# Revit family: Weitspannkabelleiter - WKLG 1160 FT,FS,FSK,FTSO,A2,A4
name_source: partatom
category: Generic Models
revit_build: Autodesk Revit 2017 (Build: 20190508_0315(x64)
units: mm (PartAtom-declared; Revit-internal decimal feet)

## family parameters
Always vertical = Yes
Can host rebar = No
Cut with Voids When Loaded = No
Part Type = Normal
Room Calculation Point = No
Round Connector Dimension = Use Diameter
Shared = No
Work Plane-Based = No

## types (6) — shared parameters
Cut's space = 75 mm
Cut's space 2 = 300 mm  [stored 0.984252 ft]
Cut's space 3 = 3000 mm  [stored 9.84252 ft]
Height = 110 mm  [stored 0.360892 ft]
Height 1 = 168 mm  [stored 0.551181 ft]
Length 1 = 773 mm  [stored 2.53609 ft]
Manufacturer = OBO Bettermann
URL = http://www.obo-bettermann.com
Width = 35 mm  [stored 0.114829 ft]
Width 1 = 600 mm
Width 2 = 300 mm  [stored 0.984252 ft]

## per-type parameters (varying)
| type | Cut's number | Cut's number 2 | Cut's number 3 | GTIN | Length | Manufacturer Art.No. | Material |
| WKLG 1160 FT | 120 | 30 | 3 | 4012196883578 | 9000 mm | 6311075 | Hot-dip galvanised |
| WKLG 1160 FS | 80 | 20 | 2 | 4012196883271 | 6000 mm  [stored 19.685 ft] | 6311024 | Strip-galvanised |
| WKLG 1160 FT SO | 80 | 20 | 2 | 4012195753056 | 6000 mm  [stored 19.685 ft] | 7189022 | Hot-dip galvanised 85 µm |
| WKLG 1160 A2 | 80 | 20 | 2 | 4012195037323 | 6000 mm  [stored 19.685 ft] | 6311218 | Hot-dip galvanised 85 µm |
| WKLG 1160 A4 | 80 | 20 | 2 | 4012195403142 | 6000 mm  [stored 19.685 ft] | 6311233 | Stainless steel, A4 |
| WKLG 1160 FSK | 80 | 20 | 2 | 4012195238836 | 6000 mm  [stored 19.685 ft] | 6479818 | PES50 - Polyester / epoxy |

note: column(s) folded — value = type name in every type: Article Type

note: [stored X ft] marks values corroborated as IEEE doubles in the binary element streams (Revit-internal decimal feet)

## geometry (parser evidence)
native form markers: Sweep x1
no freeform markers — native parametric forms only
